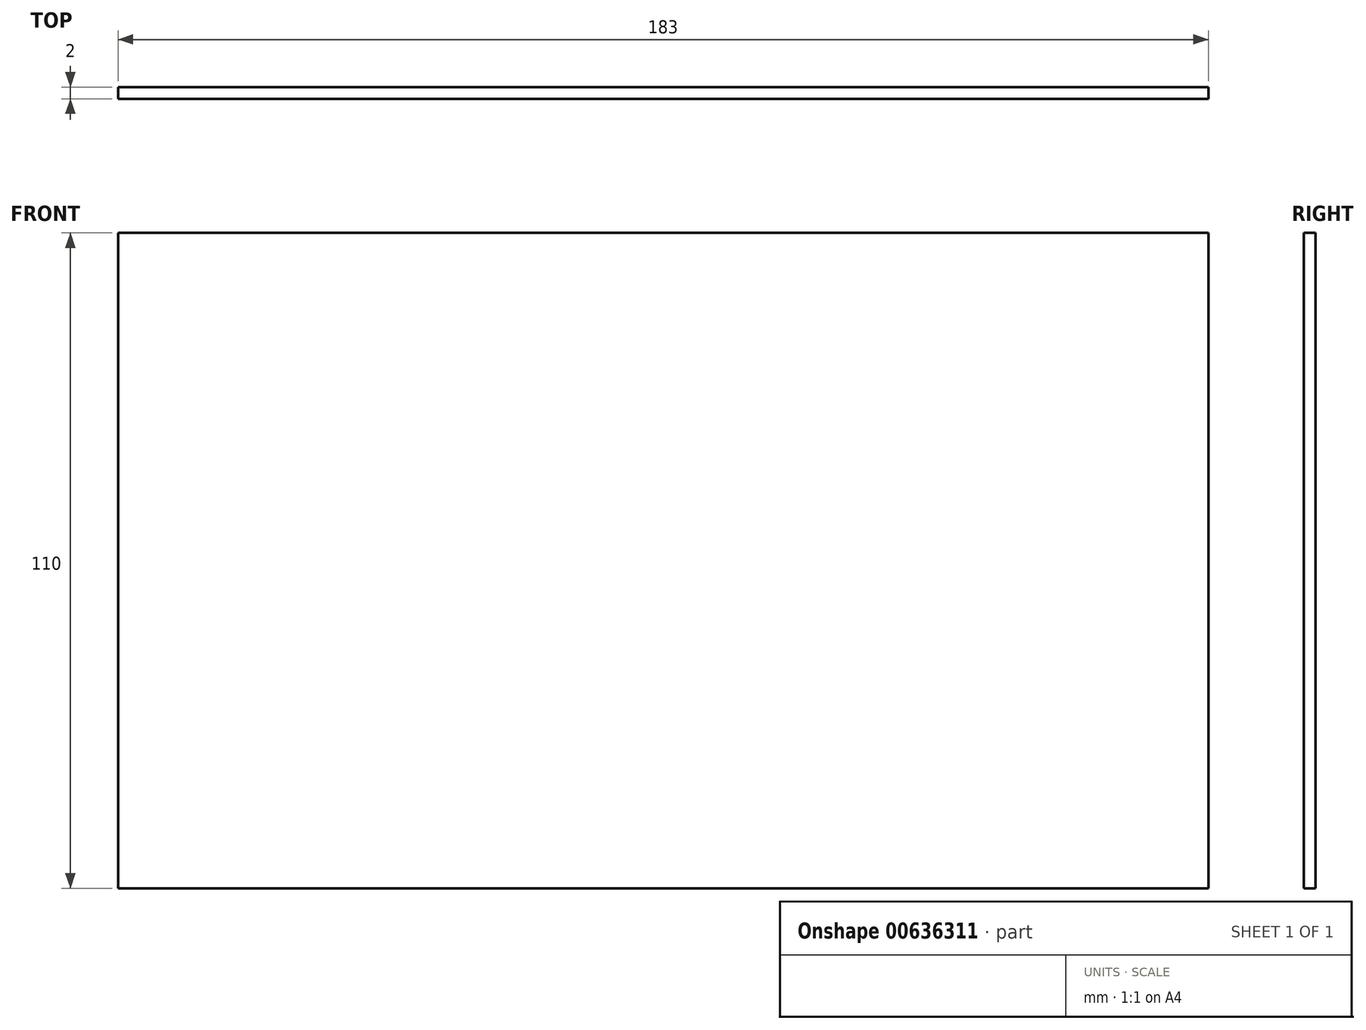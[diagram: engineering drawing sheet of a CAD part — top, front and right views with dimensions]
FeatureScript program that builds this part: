
annotation { "Feature Type Name" : "Feature", "Feature Type Description" : "" }
export const myFeature = defineFeature(function(context is Context, id is Id, definition is map)
    precondition{}
    {
        {
            var Q0;
            Q0=qCreatedBy(makeId("Front.planeOp"),FACE);
            var sketch = newSketch(context, id + "F0", { "sketchPlane" : qUnion([Q0])});
            skLineSegment(sketch, "E0.bottom", {"start": v(0, 0) * mm, "end": v(183, 0) * mm});
            skLineSegment(sketch, "E0.top", {"start": v(0, 110) * mm, "end": v(183, 110) * mm});
            skLineSegment(sketch, "E0.left", {"start": v(0, 0) * mm, "end": v(0, 110) * mm});
            skLineSegment(sketch, "E0.right", {"start": v(183, 0) * mm, "end": v(183, 110) * mm});
            skSolve(sketch);
        }
        {
            var Q0;
            Q0=qSketchRegion(id+"F0",true);
            extrude(context, id + "F1", {"entities" : qUnion([Q0]), "depth" : 2 * mm, "offsetDistance" : 25 * mm});
        }
    });
